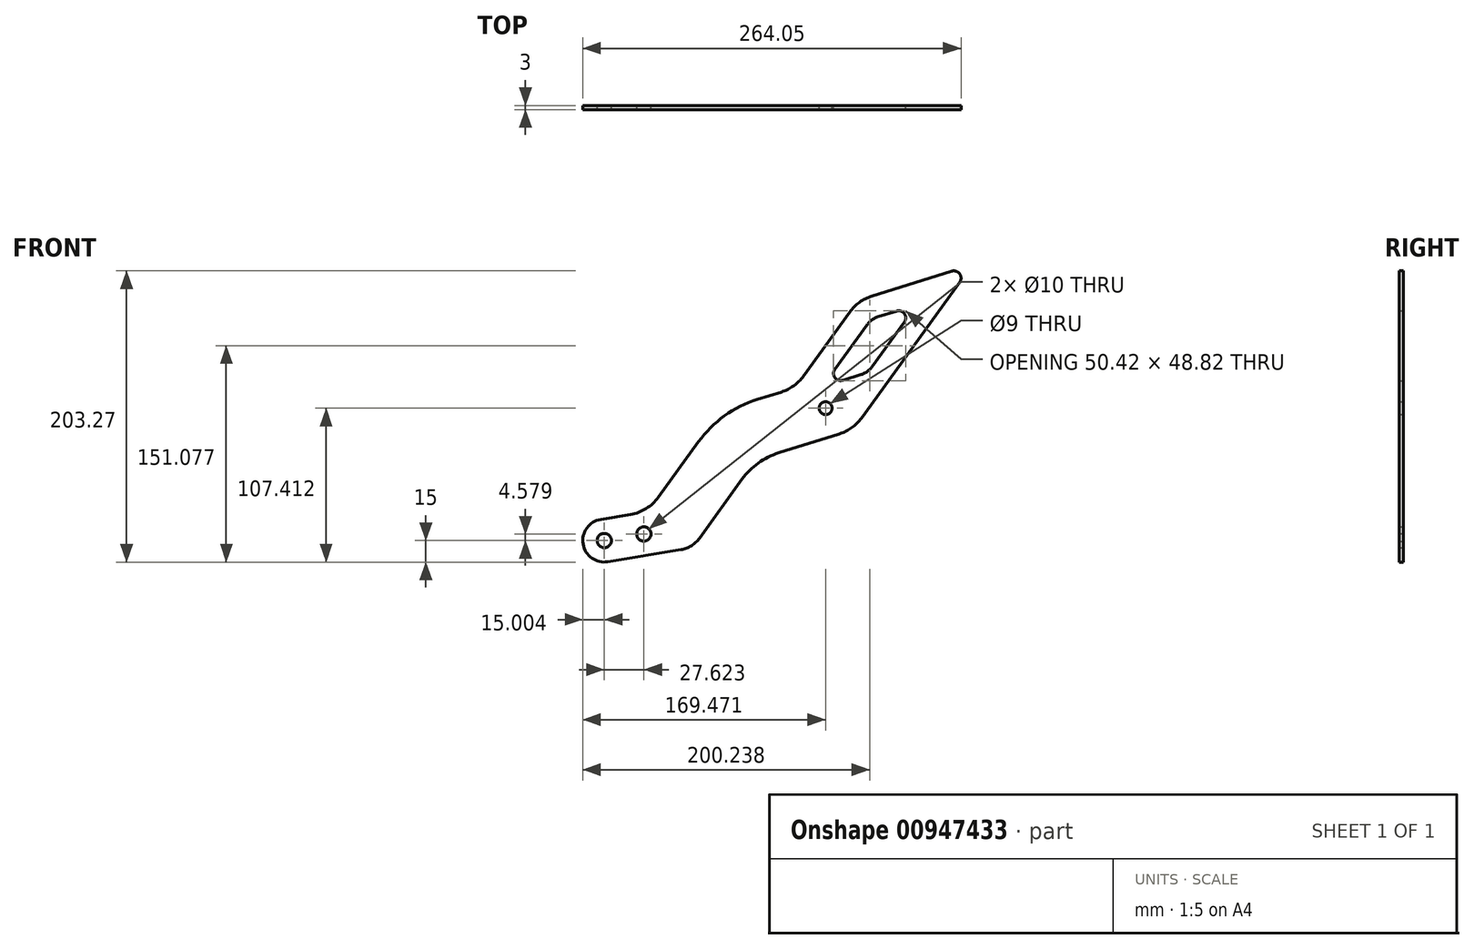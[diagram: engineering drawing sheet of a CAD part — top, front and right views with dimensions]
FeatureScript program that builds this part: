
annotation { "Feature Type Name" : "Feature", "Feature Type Description" : "" }
export const myFeature = defineFeature(function(context is Context, id is Id, definition is map)
    precondition{}
    {
        {
            var Q0;
            Q0=qCreatedBy(makeId("Front.planeOp"),FACE);
            var sketch = newSketch(context, id + "F0", { "sketchPlane" : qUnion([Q0])});
            skLineSegment(sketch, "E0", {"start": v(163.48, 86.4) * mm, "end": v(191.1, 90.99) * mm, "construction": true});
            skCircle(sketch, "E1", {"center": v(163.48, 86.4) * mm, "radius": 5 * mm});
            skCircle(sketch, "E2", {"center": v(191.1, 90.99) * mm, "radius": 5 * mm});
            skArc(sketch, "E3", {"start": v(161.03, 101.2) * mm, "mid": v(148.69, 83.96) * mm, "end": v(165.94, 71.61) * mm});
            skLineSegment(sketch, "E4", {"start": v(165.94, 71.61) * mm, "end": v(217.01, 80.08) * mm});
            skLineSegment(sketch, "E5", {"start": v(161.03, 101.2) * mm, "end": v(181.86, 104.66) * mm});
            skLineSegment(sketch, "E6", {"start": v(291.24, 313.66) * mm, "end": v(196.24, 182.3) * mm, "construction": true});
            skLineSegment(sketch, "E7.0", {"start": v(229.95, 88.09) * mm, "end": v(259.72, 129.25) * mm});
            skLineSegment(sketch, "E8.trimOffspring", {"start": v(201.26, 116.68) * mm, "end": v(229.25, 155.38) * mm});
            skPoint(sketch, "E9.visualSharp", {"position": v(225.13, 81.42) * mm});
            skArc(sketch, "E9.filletArc", {"start": v(217.01, 80.08) * mm, "mid": v(224.27, 82.8) * mm, "end": v(229.95, 88.09) * mm});
            skPoint(sketch, "E10.visualSharp", {"position": v(194.03, 106.68) * mm});
            skArc(sketch, "E10.filletArc", {"start": v(181.86, 104.66) * mm, "mid": v(192.75, 108.75) * mm, "end": v(201.26, 116.68) * mm});
            skLineSegment(sketch, "E11", {"start": v(71.42, 159.51) * mm, "end": v(187.14, 195.68) * mm, "construction": true});
            skLineSegment(sketch, "E12.0", {"start": v(285.32, 147.67) * mm, "end": v(327.67, 160.9) * mm});
            skLineSegment(sketch, "E13.0", {"start": v(270.21, 184.86) * mm, "end": v(287.1, 190.14) * mm});
            skPoint(sketch, "E14.visualSharp", {"position": v(244.83, 176.93) * mm});
            skArc(sketch, "E14.filletArc", {"start": v(270.21, 184.86) * mm, "mid": v(247.35, 173.43) * mm, "end": v(229.25, 155.38) * mm});
            skPoint(sketch, "E15.visualSharp", {"position": v(269.46, 142.71) * mm});
            skArc(sketch, "E15.filletArc", {"start": v(285.32, 147.67) * mm, "mid": v(271.03, 140.53) * mm, "end": v(259.72, 129.25) * mm});
            skLineSegment(sketch, "E16.0", {"start": v(279.35, 166.76) * mm, "end": v(458.98, 222.9) * mm, "construction": true});
            skCircle(sketch, "E17", {"center": v(317.95, 178.82) * mm, "radius": 4.5 * mm});
            skLineSegment(sketch, "E18", {"start": v(411.58, 266.75) * mm, "end": v(343.03, 171.96) * mm});
            skLineSegment(sketch, "E19.0", {"start": v(334.83, 245.94) * mm, "end": v(302.46, 201.19) * mm});
            skLineSegment(sketch, "E20", {"start": v(317.95, 178.82) * mm, "end": v(364.83, 243.65) * mm, "construction": true});
            skLineSegment(sketch, "E21.0", {"start": v(350.19, 257) * mm, "end": v(406.04, 274.45) * mm});
            skPoint(sketch, "E22.visualSharp", {"position": v(337.18, 163.88) * mm});
            skArc(sketch, "E22.filletArc", {"start": v(327.67, 160.9) * mm, "mid": v(336.24, 165.19) * mm, "end": v(343.03, 171.96) * mm});
            skPoint(sketch, "E23.visualSharp", {"position": v(296.62, 193.1) * mm});
            skArc(sketch, "E23.filletArc", {"start": v(287.1, 190.14) * mm, "mid": v(295.68, 194.42) * mm, "end": v(302.46, 201.19) * mm});
            skPoint(sketch, "E24.visualSharp", {"position": v(420.4, 278.94) * mm});
            skArc(sketch, "E24.filletArc", {"start": v(411.58, 266.75) * mm, "mid": v(411.59, 272.6) * mm, "end": v(406.04, 274.45) * mm});
            skPoint(sketch, "E25.visualSharp", {"position": v(340.67, 254.02) * mm});
            skArc(sketch, "E25.filletArc", {"start": v(350.19, 257) * mm, "mid": v(341.61, 252.71) * mm, "end": v(334.83, 245.94) * mm});
            skLineSegment(sketch, "E26.0", {"start": v(354.66, 242.68) * mm, "end": v(367.44, 246.67) * mm});
            skLineSegment(sketch, "E27.0", {"start": v(372.98, 238.97) * mm, "end": v(350.45, 207.82) * mm});
            skLineSegment(sketch, "E28.0", {"start": v(346.98, 237.15) * mm, "end": v(324.46, 206) * mm});
            skLineSegment(sketch, "E29", {"start": v(342.77, 202.3) * mm, "end": v(330, 198.3) * mm});
            skPoint(sketch, "E30.visualSharp", {"position": v(349.9, 241.2) * mm});
            skArc(sketch, "E30.filletArc", {"start": v(354.66, 242.68) * mm, "mid": v(350.38, 240.54) * mm, "end": v(346.98, 237.15) * mm});
            skPoint(sketch, "E31.visualSharp", {"position": v(347.53, 203.78) * mm});
            skArc(sketch, "E31.filletArc", {"start": v(342.77, 202.3) * mm, "mid": v(347.06, 204.44) * mm, "end": v(350.45, 207.82) * mm});
            skPoint(sketch, "E32.visualSharp", {"position": v(381.8, 251.16) * mm});
            skArc(sketch, "E32.filletArc", {"start": v(372.98, 238.97) * mm, "mid": v(372.99, 244.82) * mm, "end": v(367.44, 246.67) * mm});
            skPoint(sketch, "E33.visualSharp", {"position": v(315.64, 193.82) * mm});
            skArc(sketch, "E33.filletArc", {"start": v(324.46, 206) * mm, "mid": v(324.45, 200.15) * mm, "end": v(330, 198.3) * mm});
            skSolve(sketch);
        }
        {
            var Q0;
            Q0 = qSketchRegion(id + "F0", true);
            extrude(context, id + "F1", {"entities" : qUnion([Q0]), "depth" : 3 * mm, "offsetDistance" : 25 * mm});
        }
    });
